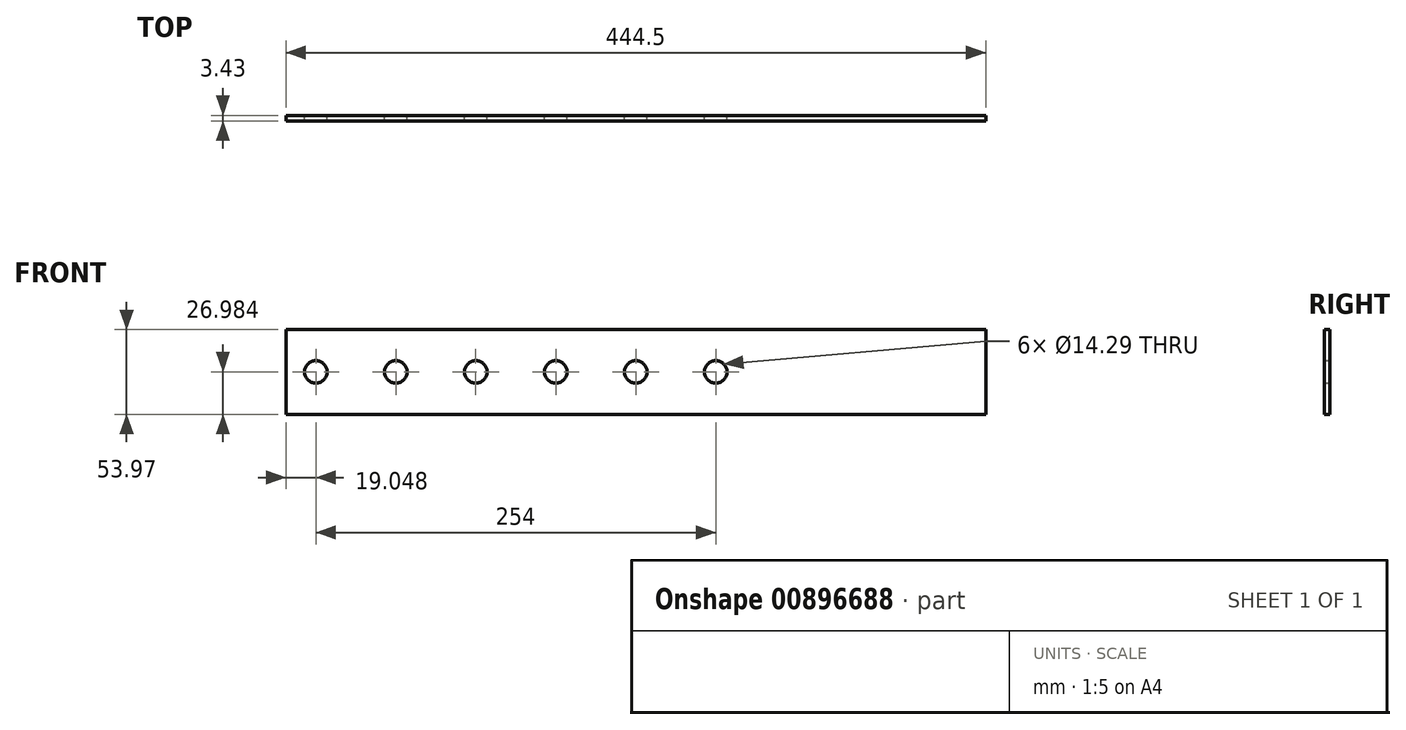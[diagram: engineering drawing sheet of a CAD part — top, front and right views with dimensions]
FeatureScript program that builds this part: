
annotation { "Feature Type Name" : "Feature", "Feature Type Description" : "" }
export const myFeature = defineFeature(function(context is Context, id is Id, definition is map)
    precondition{}
    {
        {
            var Q0;
            Q0=qCreatedBy(makeId("Front.planeOp"),FACE);
            var sketch = newSketch(context, id + "F0", { "sketchPlane" : qUnion([Q0])});
            skCircle(sketch, "E0", {"center": v(-687.41, 551.04) * mm, "radius": 7.14 * mm});
            skCircle(sketch, "E1", {"center": v(-636.61, 551.04) * mm, "radius": 7.14 * mm});
            skCircle(sketch, "E2", {"center": v(-585.81, 551.04) * mm, "radius": 7.14 * mm});
            skCircle(sketch, "E3", {"center": v(-535.01, 551.04) * mm, "radius": 7.14 * mm});
            skCircle(sketch, "E4", {"center": v(-484.21, 551.04) * mm, "radius": 7.14 * mm});
            skCircle(sketch, "E5", {"center": v(-433.41, 551.04) * mm, "radius": 7.14 * mm});
            skLineSegment(sketch, "E6", {"start": v(-706.46, 524.06) * mm, "end": v(-261.96, 524.06) * mm});
            skLineSegment(sketch, "E7", {"start": v(-706.46, 578.03) * mm, "end": v(-706.46, 524.06) * mm});
            skLineSegment(sketch, "E8", {"start": v(-261.96, 578.03) * mm, "end": v(-706.46, 578.03) * mm});
            skLineSegment(sketch, "E9", {"start": v(-261.96, 524.06) * mm, "end": v(-261.96, 578.03) * mm});
            skSolve(sketch);
        }
        {
            var Q0;
            Q0 = qSketchRegion(id + "F0", true);
            extrude(context, id + "F1", {"entities" : qUnion([Q0]), "depth" : 3.43 * mm, "offsetDistance" : 25.4 * mm});
        }
    });
